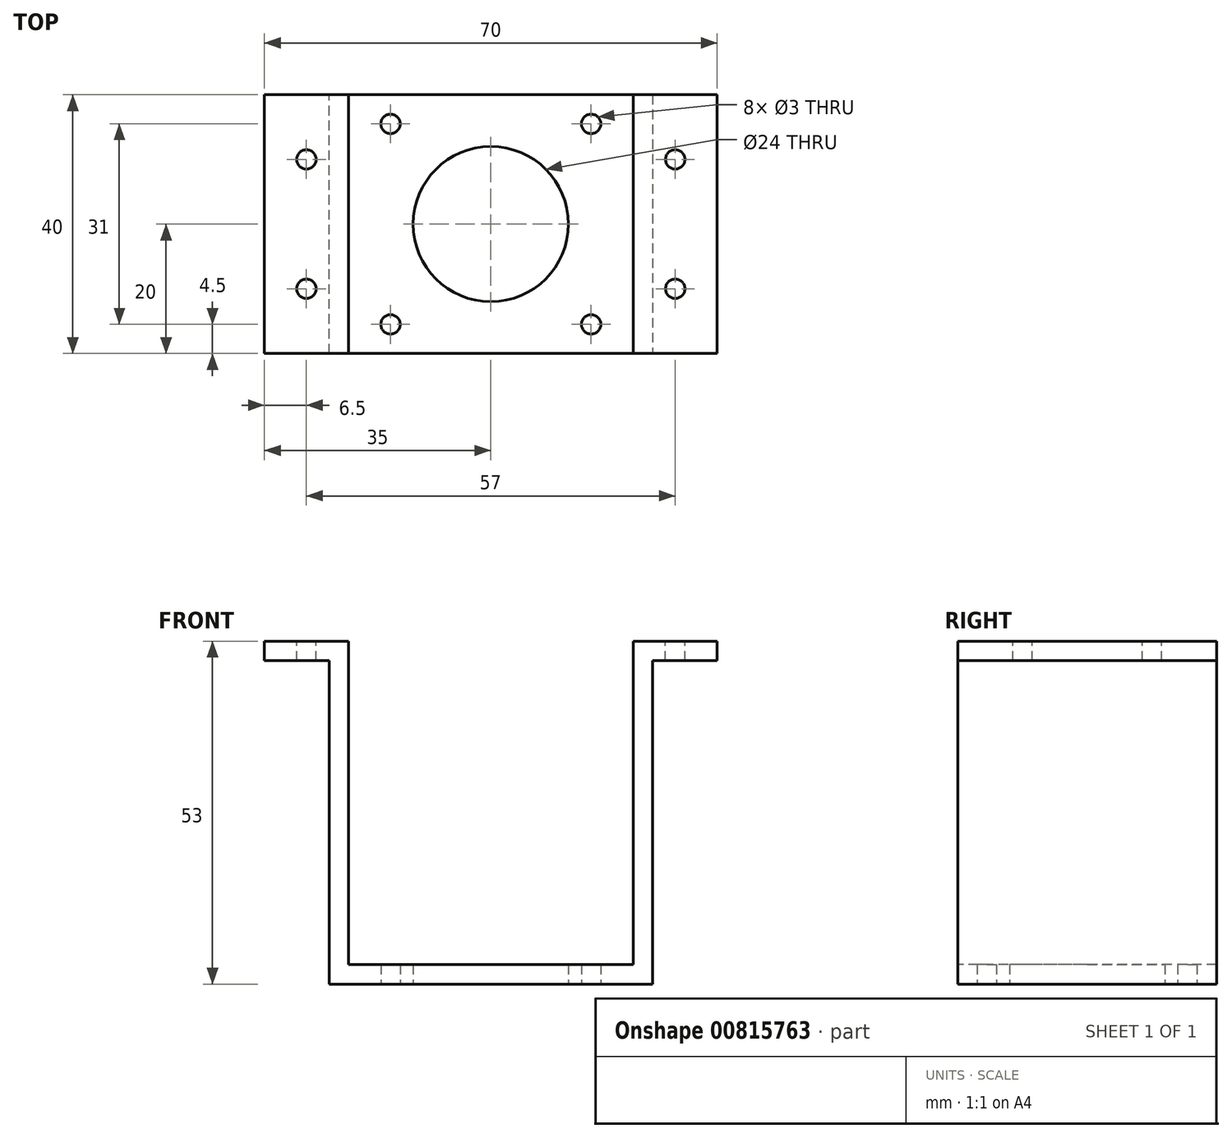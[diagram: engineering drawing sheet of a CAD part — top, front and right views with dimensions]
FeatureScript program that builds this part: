
annotation { "Feature Type Name" : "Feature", "Feature Type Description" : "" }
export const myFeature = defineFeature(function(context is Context, id is Id, definition is map)
    precondition{}
    {
        {
            var Q0;
            Q0=qCreatedBy(makeId("Top.planeOp"),FACE);
            var sketch = newSketch(context, id + "F0", { "sketchPlane" : qUnion([Q0])});
            skLineSegment(sketch, "E0.bottom", {"start": v(25, -20) * mm, "end": v(-25, -20) * mm});
            skLineSegment(sketch, "E0.top", {"start": v(25, 20) * mm, "end": v(-25, 20) * mm});
            skLineSegment(sketch, "E0.left", {"start": v(25, -20) * mm, "end": v(25, 20) * mm});
            skLineSegment(sketch, "E0.right", {"start": v(-25, -20) * mm, "end": v(-25, 20) * mm});
            skPoint(sketch, "E0.middle", {"position": v(0, 0) * mm});
            skSolve(sketch);
        }
        {
            var Q0;
            Q0 = qSketchRegion(id + "F0", true);
            extrude(context, id + "F1", {"entities" : qUnion([Q0]), "depth" : 3 * mm, "offsetDistance" : 25 * mm});
        }
        {
            var Q0;
            Q0=makeQuery(id+"F1.opExtrude","CAP_FACE",FACE,{"disambiguationData":[OSD([sQuery(id+"F0.wireOp",EDGE,"E0.bottom"),sQuery(id+"F0.wireOp",EDGE,"E0.top"),sQuery(id+"F0.wireOp",EDGE,"E0.left"),sQuery(id+"F0.wireOp",EDGE,"E0.right")])],"isStart":false});
            var sketch = newSketch(context, id + "F2", { "sketchPlane" : qUnion([Q0])});
            skLineSegment(sketch, "E1.bottom", {"start": v(-25, 20) * mm, "end": v(-22, 20) * mm});
            skLineSegment(sketch, "E1.top", {"start": v(-25, -20) * mm, "end": v(-22, -20) * mm});
            skLineSegment(sketch, "E1.left", {"start": v(-25, 20) * mm, "end": v(-25, -20) * mm});
            skLineSegment(sketch, "E1.right", {"start": v(-22, 20) * mm, "end": v(-22, -20) * mm});
            skLineSegment(sketch, "E2.bottom", {"start": v(25, 20) * mm, "end": v(22, 20) * mm});
            skLineSegment(sketch, "E2.top", {"start": v(25, -20) * mm, "end": v(22, -20) * mm});
            skLineSegment(sketch, "E2.left", {"start": v(25, 20) * mm, "end": v(25, -20) * mm});
            skLineSegment(sketch, "E2.right", {"start": v(22, 20) * mm, "end": v(22, -20) * mm});
            skSolve(sketch);
        }
        {
            var Q0;
            Q0=makeQuery(id+"F2.imprint","IMPRINT",FACE,{"disambiguationData":[TD([[makeQuery(id+"F2.imprint","IMPRINT",EDGE,{"derivedFrom":sQuery(id+"F2.wireOp",EDGE,"E2.bottom")}),1.0]])]});
            var Q1;
            Q1=makeQuery(id+"F2.imprint","IMPRINT",FACE,{"disambiguationData":[TD([[makeQuery(id+"F2.imprint","IMPRINT",EDGE,{"derivedFrom":sQuery(id+"F2.wireOp",EDGE,"E1.bottom")}),1.0]])]});
            extrude(context, id + "F3", {"entities" : qUnion([Q0, Q1]), "operationType" : NewBodyOperationType.ADD, "depth" : 50 * mm, "offsetDistance" : 25 * mm});
        }
        {
            var Q0;
            Q0=makeQuery(id+"F3.boolean.opBoolean","MERGE",FACE,{"derivedFrom":[makeQuery(id+"F1.opExtrude","SWEPT_FACE",FACE,{"disambiguationData":[OSD([sQuery(id+"F0.wireOp",EDGE,"E0.left")])]}),makeQuery(id+"F3.opExtrude","SWEPT_FACE",FACE,{"disambiguationData":[OSD([sQuery(id+"F2.wireOp",EDGE,"E2.left")])]})]});
            var sketch = newSketch(context, id + "F4", { "sketchPlane" : qUnion([Q0])});
            skLineSegment(sketch, "E3.bottom", {"start": v(20, 53) * mm, "end": v(-20, 53) * mm});
            skLineSegment(sketch, "E3.top", {"start": v(20, 50) * mm, "end": v(-20, 50) * mm});
            skLineSegment(sketch, "E3.left", {"start": v(20, 53) * mm, "end": v(20, 50) * mm});
            skLineSegment(sketch, "E3.right", {"start": v(-20, 53) * mm, "end": v(-20, 50) * mm});
            skSolve(sketch);
        }
        {
            var Q0;
            Q0=makeQuery(id+"F4.imprint","IMPRINT",FACE,{"disambiguationData":[TD([[makeQuery(id+"F4.imprint","IMPRINT",EDGE,{"derivedFrom":sQuery(id+"F4.wireOp",EDGE,"E3.bottom")}),-1.0]])]});
            extrude(context, id + "F5", {"entities" : qUnion([Q0]), "operationType" : NewBodyOperationType.ADD, "depth" : 10 * mm, "offsetDistance" : 25 * mm});
        }
        {
            var Q0;
            Q0=makeQuery(id+"F3.boolean.opBoolean","MERGE",FACE,{"derivedFrom":[makeQuery(id+"F1.opExtrude","SWEPT_FACE",FACE,{"disambiguationData":[OSD([sQuery(id+"F0.wireOp",EDGE,"E0.right")])]}),makeQuery(id+"F3.opExtrude","SWEPT_FACE",FACE,{"disambiguationData":[OSD([sQuery(id+"F2.wireOp",EDGE,"E1.left")])]})]});
            var sketch = newSketch(context, id + "F6", { "sketchPlane" : qUnion([Q0])});
            skLineSegment(sketch, "E4.bottom", {"start": v(20, 53) * mm, "end": v(-20, 53) * mm});
            skLineSegment(sketch, "E4.top", {"start": v(20, 50) * mm, "end": v(-20, 50) * mm});
            skLineSegment(sketch, "E4.left", {"start": v(20, 53) * mm, "end": v(20, 50) * mm});
            skLineSegment(sketch, "E4.right", {"start": v(-20, 53) * mm, "end": v(-20, 50) * mm});
            skSolve(sketch);
        }
        {
            var Q0;
            Q0 = qSketchRegion(id + "F6", true);
            extrude(context, id + "F7", {"entities" : qUnion([Q0]), "operationType" : NewBodyOperationType.ADD, "depth" : 10 * mm, "offsetDistance" : 25 * mm});
        }
        {
            var Q0;
            Q0=makeQuery(id+"F1.opExtrude","CAP_FACE",FACE,{"disambiguationData":[OSD([sQuery(id+"F0.wireOp",EDGE,"E0.bottom"),sQuery(id+"F0.wireOp",EDGE,"E0.top"),sQuery(id+"F0.wireOp",EDGE,"E0.left"),sQuery(id+"F0.wireOp",EDGE,"E0.right")])],"isStart":true});
            var sketch = newSketch(context, id + "F8", { "sketchPlane" : qUnion([Q0])});
            skLineSegment(sketch, "E5.bottom", {"start": v(15.5, -15.5) * mm, "end": v(-15.5, -15.5) * mm});
            skLineSegment(sketch, "E5.top", {"start": v(15.5, 15.5) * mm, "end": v(-15.5, 15.5) * mm});
            skLineSegment(sketch, "E5.left", {"start": v(15.5, -15.5) * mm, "end": v(15.5, 15.5) * mm});
            skLineSegment(sketch, "E5.right", {"start": v(-15.5, -15.5) * mm, "end": v(-15.5, 15.5) * mm});
            skPoint(sketch, "E5.middle", {"position": v(0, 0) * mm});
            skCircle(sketch, "E6", {"center": v(0, 0) * mm, "radius": 12 * mm});
            skSolve(sketch);
        }
        {
            var Q0;
            Q0=sQuery(id+"F8.wireOp",VERTEX,"E5.top.end");
            var Q1;
            Q1=sQuery(id+"F8.wireOp",VERTEX,"E5.top.start");
            var Q2;
            Q2=sQuery(id+"F8.wireOp",VERTEX,"E5.bottom.start");
            var Q3;
            Q3=sQuery(id+"F8.wireOp",VERTEX,"E5.bottom.end");
            var Q4;
            Q4=makeQuery(id+"F1.opExtrude","SWEPT_BODY",BODY,{"disambiguationData":[OSD([sQuery(id+"F0.wireOp",EDGE,"E0.bottom"),sQuery(id+"F0.wireOp",EDGE,"E0.top"),sQuery(id+"F0.wireOp",EDGE,"E0.left"),sQuery(id+"F0.wireOp",EDGE,"E0.right")])]});
            hole(context, id + "F9", {"style" : HoleStyle.SIMPLE, "endStyle" : HoleEndStyle.THROUGH, "holeDiameter" : 3 * mm, "majorDiameter" : 5 * mm, "isTappedThrough" : true, "tappedDepth" : 12 * mm, "tapClearance" : 3, "locations" : qUnion([Q0, Q1, Q2, Q3]), "scope" : qUnion([Q4])});
        }
        {
            var Q0;
            Q0=makeQuery(id+"F8.imprint","IMPRINT",FACE,{"disambiguationData":[TD([[makeQuery(id+"F8.imprint","IMPRINT",EDGE,{"derivedFrom":sQuery(id+"F8.wireOp",EDGE,"E6")}),1.0]])]});
            extrude(context, id + "F10", {"entities" : qUnion([Q0]), "operationType" : NewBodyOperationType.REMOVE, "oppositeDirection" : true, "depth" : 25 * mm, "offsetDistance" : 25 * mm});
        }
        {
            var Q0;
            Q0=makeQuery(id+"F7.boolean.opBoolean","MERGE",FACE,{"derivedFrom":[makeQuery(id+"F3.opExtrude","CAP_FACE",FACE,{"disambiguationData":[OSD([sQuery(id+"F2.wireOp",EDGE,"E1.bottom"),sQuery(id+"F2.wireOp",EDGE,"E1.top"),sQuery(id+"F2.wireOp",EDGE,"E1.left"),sQuery(id+"F2.wireOp",EDGE,"E1.right")])],"isStart":false}),makeQuery(id+"F7.opExtrude","SWEPT_FACE",FACE,{"disambiguationData":[OSD([sQuery(id+"F6.wireOp",EDGE,"E4.bottom")])]})]});
            var sketch = newSketch(context, id + "F11", { "sketchPlane" : qUnion([Q0])});
            skLineSegment(sketch, "E7", {"start": v(-28.5, 10) * mm, "end": v(-28.5, -10) * mm});
            skPoint(sketch, "E7.startSnap0", {"position": v(-28.5, 20) * mm});
            skSolve(sketch);
        }
        {
            var Q0;
            Q0=sQuery(id+"F11.wireOp",VERTEX,"E7.end");
            var Q1;
            Q1=sQuery(id+"F11.wireOp",VERTEX,"E7.start");
            var Q2;
            Q2=makeQuery(id+"F1.opExtrude","SWEPT_BODY",BODY,{"disambiguationData":[OSD([sQuery(id+"F0.wireOp",EDGE,"E0.bottom"),sQuery(id+"F0.wireOp",EDGE,"E0.top"),sQuery(id+"F0.wireOp",EDGE,"E0.left"),sQuery(id+"F0.wireOp",EDGE,"E0.right")])]});
            hole(context, id + "F12", {"style" : HoleStyle.SIMPLE, "endStyle" : HoleEndStyle.THROUGH, "holeDiameter" : 3 * mm, "majorDiameter" : 5 * mm, "isTappedThrough" : true, "tappedDepth" : 12 * mm, "tapClearance" : 3, "locations" : qUnion([Q0, Q1]), "scope" : qUnion([Q2])});
        }
        {
            var Q0;
            Q0=makeQuery(id+"F5.boolean.opBoolean","MERGE",FACE,{"derivedFrom":[makeQuery(id+"F3.opExtrude","CAP_FACE",FACE,{"disambiguationData":[OSD([sQuery(id+"F2.wireOp",EDGE,"E2.bottom"),sQuery(id+"F2.wireOp",EDGE,"E2.top"),sQuery(id+"F2.wireOp",EDGE,"E2.left"),sQuery(id+"F2.wireOp",EDGE,"E2.right")])],"isStart":false}),makeQuery(id+"F5.opExtrude","SWEPT_FACE",FACE,{"disambiguationData":[OSD([sQuery(id+"F4.wireOp",EDGE,"E3.bottom")])]})]});
            var sketch = newSketch(context, id + "F13", { "sketchPlane" : qUnion([Q0])});
            skLineSegment(sketch, "E8", {"start": v(28.5, 10) * mm, "end": v(28.5, -10) * mm});
            skPoint(sketch, "E8.startSnap0", {"position": v(28.5, 20) * mm});
            skSolve(sketch);
        }
        {
            var Q0;
            Q0=sQuery(id+"F13.wireOp",VERTEX,"E8.start");
            var Q1;
            Q1=sQuery(id+"F13.wireOp",VERTEX,"E8.end");
            var Q2;
            Q2=makeQuery(id+"F1.opExtrude","SWEPT_BODY",BODY,{"disambiguationData":[OSD([sQuery(id+"F0.wireOp",EDGE,"E0.bottom"),sQuery(id+"F0.wireOp",EDGE,"E0.top"),sQuery(id+"F0.wireOp",EDGE,"E0.left"),sQuery(id+"F0.wireOp",EDGE,"E0.right")])]});
            hole(context, id + "F14", {"style" : HoleStyle.SIMPLE, "endStyle" : HoleEndStyle.THROUGH, "holeDiameter" : 3 * mm, "majorDiameter" : 5 * mm, "isTappedThrough" : true, "tappedDepth" : 12 * mm, "tapClearance" : 3, "locations" : qUnion([Q0, Q1]), "scope" : qUnion([Q2])});
        }
    });
